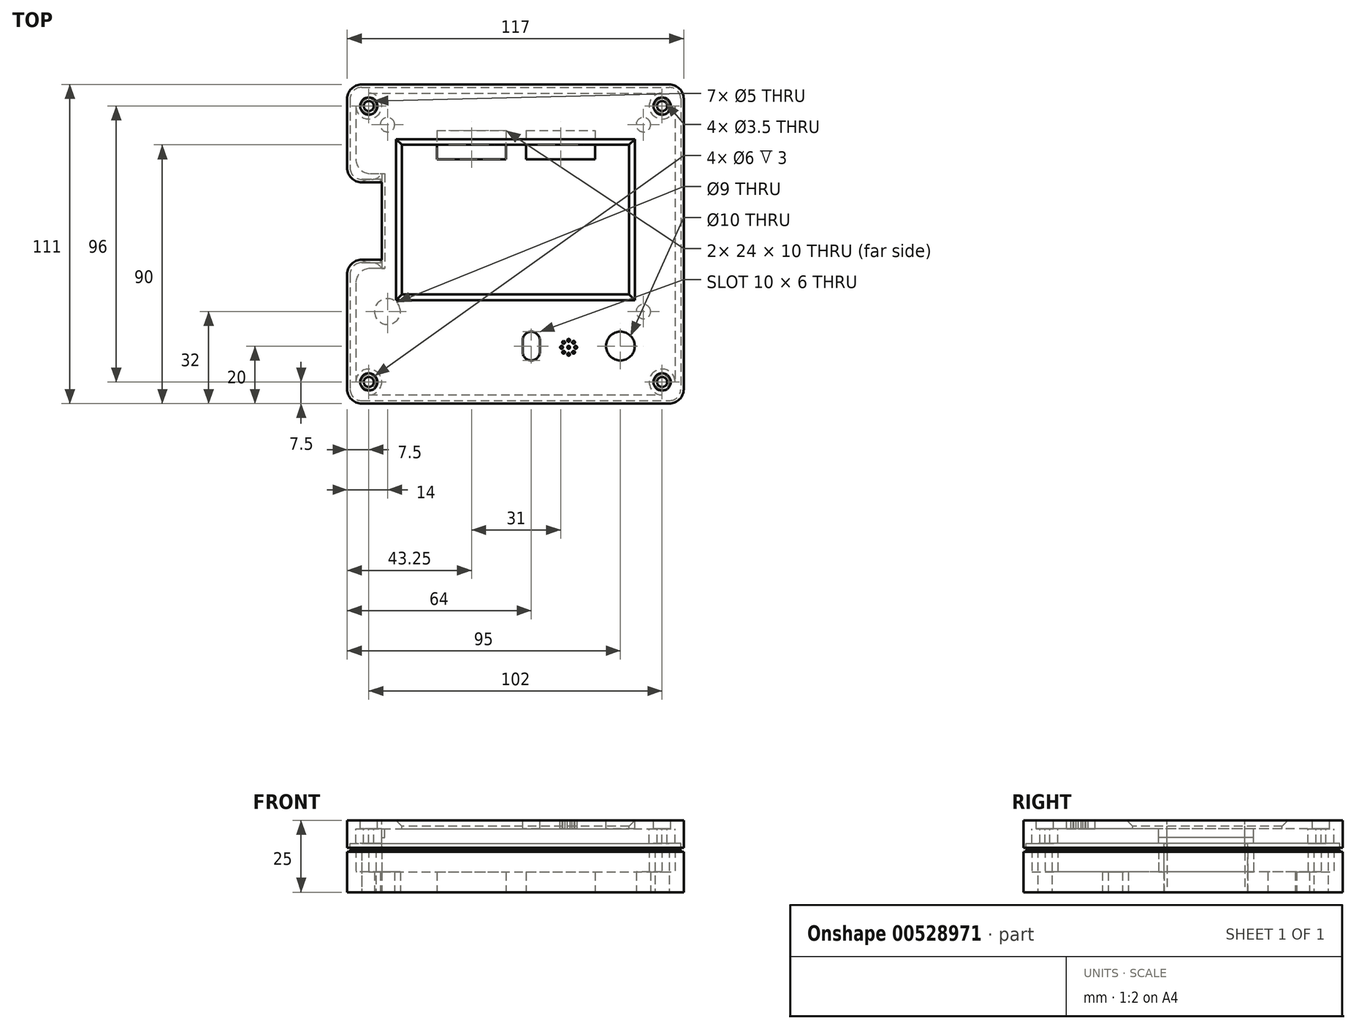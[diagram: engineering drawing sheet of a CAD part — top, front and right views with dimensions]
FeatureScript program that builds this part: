
annotation { "Feature Type Name" : "Feature", "Feature Type Description" : "" }
export const myFeature = defineFeature(function(context is Context, id is Id, definition is map)
    precondition{}
    {
        {
            var Q0;
            Q0=qCreatedBy(makeId("Top.planeOp"),FACE);
            var sketch = newSketch(context, id + "F0", { "sketchPlane" : qUnion([Q0])});
            skLineSegment(sketch, "E0.bottom", {"start": v(-46.5, 43.5) * mm, "end": v(46.5, 43.5) * mm});
            skLineSegment(sketch, "E0.top", {"start": v(-46.5, -43.5) * mm, "end": v(46.5, -43.5) * mm});
            skLineSegment(sketch, "E0.left", {"start": v(-46.5, 43.5) * mm, "end": v(-46.5, -43.5) * mm});
            skLineSegment(sketch, "E0.right", {"start": v(46.5, 43.5) * mm, "end": v(46.5, -43.5) * mm});
            skLineSegment(sketch, "E1.bottom", {"start": v(-51, 52.5) * mm, "end": v(51, 52.5) * mm});
            skLineSegment(sketch, "E1.top", {"start": v(-51, -52.5) * mm, "end": v(51, -52.5) * mm});
            skLineSegment(sketch, "E1.left", {"start": v(-55.5, 48) * mm, "end": v(-55.5, 29.5) * mm});
            skLineSegment(sketch, "E1.right", {"start": v(55.5, 48) * mm, "end": v(55.5, -48) * mm});
            skLineSegment(sketch, "E2.bottom", {"start": v(-53.5, 55.5) * mm, "end": v(53.5, 55.5) * mm});
            skLineSegment(sketch, "E2.top", {"start": v(-53.5, -55.5) * mm, "end": v(53.5, -55.5) * mm});
            skLineSegment(sketch, "E2.left", {"start": v(-58.5, 50.5) * mm, "end": v(-58.5, 26.5) * mm});
            skLineSegment(sketch, "E2.right", {"start": v(58.5, 50.5) * mm, "end": v(58.5, -50.5) * mm});
            skCircle(sketch, "E3", {"center": v(-51, -48) * mm, "radius": 2.5 * mm});
            skCircle(sketch, "E4", {"center": v(51, -48) * mm, "radius": 2.5 * mm});
            skCircle(sketch, "E5", {"center": v(51, 48) * mm, "radius": 2.5 * mm});
            skCircle(sketch, "E6", {"center": v(-51, 48) * mm, "radius": 2.5 * mm});
            skCircle(sketch, "E7", {"center": v(-51, 48) * mm, "radius": 4.5 * mm});
            skCircle(sketch, "E8", {"center": v(-51, -48) * mm, "radius": 4.5 * mm});
            skCircle(sketch, "E9", {"center": v(51, -48) * mm, "radius": 4.5 * mm});
            skCircle(sketch, "E10", {"center": v(51, 48) * mm, "radius": 4.5 * mm});
            skPoint(sketch, "E11.visualSharp", {"position": v(58.5, 55.5) * mm});
            skArc(sketch, "E11.filletArc", {"start": v(58.5, 50.5) * mm, "mid": v(57.04, 54.04) * mm, "end": v(53.5, 55.5) * mm});
            skPoint(sketch, "E12.visualSharp", {"position": v(58.5, -55.5) * mm});
            skArc(sketch, "E12.filletArc", {"start": v(53.5, -55.5) * mm, "mid": v(57.04, -54.04) * mm, "end": v(58.5, -50.5) * mm});
            skPoint(sketch, "E13.visualSharp", {"position": v(-58.5, -55.5) * mm});
            skArc(sketch, "E13.filletArc", {"start": v(-58.5, -50.5) * mm, "mid": v(-57.04, -54.04) * mm, "end": v(-53.5, -55.5) * mm});
            skPoint(sketch, "E14.visualSharp", {"position": v(-58.5, 55.5) * mm});
            skArc(sketch, "E14.filletArc", {"start": v(-53.5, 55.5) * mm, "mid": v(-57.04, 54.04) * mm, "end": v(-58.5, 50.5) * mm});
            skLineSegment(sketch, "E15.bottom", {"start": v(-27.25, 39.5) * mm, "end": v(-3.25, 39.5) * mm});
            skLineSegment(sketch, "E15.top", {"start": v(-27.25, 29.5) * mm, "end": v(-3.25, 29.5) * mm});
            skLineSegment(sketch, "E15.left", {"start": v(-27.25, 39.5) * mm, "end": v(-27.25, 29.5) * mm});
            skLineSegment(sketch, "E15.right", {"start": v(-3.25, 39.5) * mm, "end": v(-3.25, 29.5) * mm});
            skPoint(sketch, "E16.firstSnap0", {"position": v(-15.25, 39.5) * mm});
            skLineSegment(sketch, "E16.bottom", {"start": v(3.75, 39.5) * mm, "end": v(27.75, 39.5) * mm});
            skLineSegment(sketch, "E16.top", {"start": v(3.75, 29.5) * mm, "end": v(27.75, 29.5) * mm});
            skLineSegment(sketch, "E16.left", {"start": v(3.75, 39.5) * mm, "end": v(3.75, 29.5) * mm});
            skLineSegment(sketch, "E16.right", {"start": v(27.75, 39.5) * mm, "end": v(27.75, 29.5) * mm});
            skCircle(sketch, "E17", {"center": v(44.5, 41.5) * mm, "radius": 2.5 * mm});
            skCircle(sketch, "E18", {"center": v(44.5, -23.5) * mm, "radius": 2.5 * mm});
            skCircle(sketch, "E19", {"center": v(-44.5, -23.5) * mm, "radius": 2.5 * mm});
            skCircle(sketch, "E20", {"center": v(-44.5, 41.5) * mm, "radius": 2.5 * mm});
            skCircle(sketch, "E21", {"center": v(-44.5, 41.5) * mm, "radius": 4.5 * mm});
            skCircle(sketch, "E22", {"center": v(44.5, 41.5) * mm, "radius": 4.5 * mm});
            skCircle(sketch, "E23", {"center": v(44.5, -23.5) * mm, "radius": 4.5 * mm});
            skCircle(sketch, "E24", {"center": v(-44.5, -23.5) * mm, "radius": 4.5 * mm});
            skLineSegment(sketch, "E25.bottom", {"start": v(-46.5, 21.5) * mm, "end": v(-53.5, 21.5) * mm});
            skLineSegment(sketch, "E25.top", {"start": v(-46.5, -5.5) * mm, "end": v(-53.5, -5.5) * mm});
            skLineSegment(sketch, "E25.left", {"start": v(-46.5, 21.5) * mm, "end": v(-46.5, -5.5) * mm});
            skLineSegment(sketch, "E26.trimOffspring", {"start": v(-58.5, -10.5) * mm, "end": v(-58.5, -50.5) * mm});
            skLineSegment(sketch, "E27.trimOffspring", {"start": v(-55.5, -13.5) * mm, "end": v(-55.5, -48) * mm});
            skPoint(sketch, "E28.visualSharp", {"position": v(-58.5, 21.5) * mm});
            skArc(sketch, "E28.filletArc", {"start": v(-58.5, 26.5) * mm, "mid": v(-57.04, 22.96) * mm, "end": v(-53.5, 21.5) * mm});
            skPoint(sketch, "E29.visualSharp", {"position": v(-58.5, -5.5) * mm});
            skArc(sketch, "E29.filletArc", {"start": v(-53.5, -5.5) * mm, "mid": v(-57.04, -6.96) * mm, "end": v(-58.5, -10.5) * mm});
            skLineSegment(sketch, "E30.top", {"start": v(-46.5, -8.5) * mm, "end": v(-50.5, -8.5) * mm});
            skLineSegment(sketch, "E30.left", {"start": v(-46.5, -5.5) * mm, "end": v(-46.5, -8.5) * mm});
            skArc(sketch, "E31.filletArc", {"start": v(-50.5, -8.5) * mm, "mid": v(-54.04, -9.96) * mm, "end": v(-55.5, -13.5) * mm});
            skLineSegment(sketch, "E32", {"start": v(-50.5, 24.5) * mm, "end": v(-46.5, 24.5) * mm});
            skPoint(sketch, "E33.visualSharp", {"position": v(-55.5, 24.5) * mm});
            skArc(sketch, "E33.filletArc", {"start": v(-55.5, 29.5) * mm, "mid": v(-54.04, 25.96) * mm, "end": v(-50.5, 24.5) * mm});
            skArc(sketch, "E34.0", {"start": v(-53.5, -6.5) * mm, "mid": v(-56.33, -7.67) * mm, "end": v(-57.5, -10.5) * mm});
            skLineSegment(sketch, "E34.1", {"start": v(-57.5, -10.5) * mm, "end": v(-57.5, -50.5) * mm});
            skArc(sketch, "E34.2", {"start": v(-57.5, -50.5) * mm, "mid": v(-56.33, -53.33) * mm, "end": v(-53.5, -54.5) * mm});
            skLineSegment(sketch, "E34.3", {"start": v(-57.5, 50.5) * mm, "end": v(-57.5, 26.5) * mm});
            skArc(sketch, "E34.4", {"start": v(-57.5, 26.5) * mm, "mid": v(-56.33, 23.67) * mm, "end": v(-53.5, 22.5) * mm});
            skLineSegment(sketch, "E34.5", {"start": v(-46.5, 22.5) * mm, "end": v(-53.5, 22.5) * mm});
            skArc(sketch, "E34.7", {"start": v(-53.5, 54.5) * mm, "mid": v(-56.33, 53.33) * mm, "end": v(-57.5, 50.5) * mm});
            skLineSegment(sketch, "E34.8", {"start": v(-53.5, 54.5) * mm, "end": v(53.5, 54.5) * mm});
            skArc(sketch, "E34.9", {"start": v(57.5, 50.5) * mm, "mid": v(56.33, 53.33) * mm, "end": v(53.5, 54.5) * mm});
            skLineSegment(sketch, "E34.10", {"start": v(57.5, 50.5) * mm, "end": v(57.5, -50.5) * mm});
            skArc(sketch, "E34.11", {"start": v(53.5, -54.5) * mm, "mid": v(56.33, -53.33) * mm, "end": v(57.5, -50.5) * mm});
            skLineSegment(sketch, "E34.12", {"start": v(-53.5, -54.5) * mm, "end": v(53.5, -54.5) * mm});
            skLineSegment(sketch, "E35", {"start": v(-53.5, -6.5) * mm, "end": v(-46.5, -6.5) * mm});
            skLineSegment(sketch, "E36", {"start": v(-53.5, -5.5) * mm, "end": v(-53.5, -6.5) * mm});
            skLineSegment(sketch, "E37", {"start": v(-53.5, 22.5) * mm, "end": v(-53.5, 21.5) * mm});
            skLineSegment(sketch, "E38.bottom", {"start": v(-46.5, 24.5) * mm, "end": v(-43.5, 24.5) * mm});
            skLineSegment(sketch, "E38.top", {"start": v(-46.5, -8.5) * mm, "end": v(-43.5, -8.5) * mm});
            skLineSegment(sketch, "E38.left", {"start": v(-46.5, 24.5) * mm, "end": v(-46.5, -8.5) * mm});
            skLineSegment(sketch, "E38.right", {"start": v(-43.5, 24.5) * mm, "end": v(-43.5, -8.5) * mm});
            skSolve(sketch);
        }
        {
            var Q0;
            {var subQ0=sQuery(id+"F0.wireOp",EDGE,"E1.bottom");Q0=makeQuery(id+"F0.imprint","IMPRINT",FACE,{"disambiguationData":[TD([[makeQuery(id+"F0.imprint","IMPRINT",EDGE,{"derivedFrom":subQ0}),1.0]])]});}
            var Q1;
            Q1=makeQuery(id+"F0.imprint","IMPRINT",FACE,{"disambiguationData":[TD([[makeQuery(id+"F0.imprint","IMPRINT",EDGE,{"derivedFrom":sQuery(id+"F0.wireOp",EDGE,"E6")}),-1.0]])]});
            var Q2;
            Q2=makeQuery(id+"F0.imprint","IMPRINT",FACE,{"disambiguationData":[TD([[makeQuery(id+"F0.imprint","IMPRINT",EDGE,{"derivedFrom":sQuery(id+"F0.wireOp",EDGE,"E5")}),-1.0]])]});
            var Q3;
            Q3=makeQuery(id+"F0.imprint","IMPRINT",FACE,{"disambiguationData":[TD([[makeQuery(id+"F0.imprint","IMPRINT",EDGE,{"derivedFrom":sQuery(id+"F0.wireOp",EDGE,"E4")}),-1.0]])]});
            var Q4;
            Q4=makeQuery(id+"F0.imprint","IMPRINT",FACE,{"disambiguationData":[TD([[makeQuery(id+"F0.imprint","IMPRINT",EDGE,{"derivedFrom":sQuery(id+"F0.wireOp",EDGE,"E3")}),-1.0]])]});
            extrude(context, id + "F1", {"entities" : qUnion([Q0, Q1, Q2, Q3, Q4]), "depth" : 15 * mm});
        }
        {
            var Q0;
            {var subQ1=sQuery(id+"F0.wireOp",EDGE,"E0.left");var subQ5=sQuery(id+"F0.wireOp",EDGE,"E0.bottom");var subQ6=makeQuery(id+"F0.imprint","INTERSECT",VERTEX,{"derivedFrom":[subQ5,subQ1]});Q0=makeQuery(id+"F0.imprint","IMPRINT",FACE,{"disambiguationData":[TD([[makeQuery(id+"F0.imprint","IMPRINT",EDGE,{"disambiguationData":[TD([[subQ6,-1.0]])],"derivedFrom":subQ5}),1.0]])]});}
            var Q1;
            {var subQ0=sQuery(id+"F0.wireOp",EDGE,"E20");var subQ1=sQuery(id+"F0.wireOp",EDGE,"E0.bottom");var subQ2=makeQuery(id+"F0.imprint","INTERSECT",VERTEX,{"disambiguationData":[OD(1.0)],"derivedFrom":[subQ1,subQ0]});Q1=makeQuery(id+"F0.imprint","IMPRINT",FACE,{"disambiguationData":[TD([[makeQuery(id+"F0.imprint","IMPRINT",EDGE,{"disambiguationData":[TD([[subQ2,-1.0]])],"derivedFrom":subQ1}),-1.0]])]});}
            var Q2;
            {var subQ3=sQuery(id+"F0.wireOp",EDGE,"E22");var subQ5=sQuery(id+"F0.wireOp",EDGE,"E0.bottom");var subQ10=makeQuery(id+"F0.imprint","INTERSECT",VERTEX,{"derivedFrom":[subQ5,subQ3]});Q2=makeQuery(id+"F0.imprint","IMPRINT",FACE,{"disambiguationData":[TD([[makeQuery(id+"F0.imprint","IMPRINT",EDGE,{"disambiguationData":[TD([[subQ10,-1.0]])],"derivedFrom":subQ5}),1.0]])]});}
            var Q3;
            {var subQ0=sQuery(id+"F0.wireOp",EDGE,"E22");var subQ1=sQuery(id+"F0.wireOp",EDGE,"E0.bottom");var subQ2=makeQuery(id+"F0.imprint","INTERSECT",VERTEX,{"derivedFrom":[subQ1,subQ0]});Q3=makeQuery(id+"F0.imprint","IMPRINT",FACE,{"disambiguationData":[TD([[makeQuery(id+"F0.imprint","IMPRINT",EDGE,{"disambiguationData":[TD([[subQ2,-1.0]])],"derivedFrom":subQ1}),-1.0]])]});}
            var Q4;
            {var subQ0=sQuery(id+"F0.wireOp",EDGE,"E19");var subQ1=sQuery(id+"F0.wireOp",EDGE,"E0.top");var subQ2=makeQuery(id+"F0.imprint","INTERSECT",VERTEX,{"disambiguationData":[OD(1.0)],"derivedFrom":[subQ1,subQ0]});Q4=makeQuery(id+"F0.imprint","IMPRINT",FACE,{"disambiguationData":[TD([[makeQuery(id+"F0.imprint","IMPRINT",EDGE,{"disambiguationData":[TD([[subQ2,-1.0]])],"derivedFrom":subQ1}),1.0]])]});}
            var Q5;
            {var subQ0=sQuery(id+"F0.wireOp",EDGE,"E24");var subQ1=sQuery(id+"F0.wireOp",EDGE,"E0.left");var subQ2=makeQuery(id+"F0.imprint","INTERSECT",VERTEX,{"disambiguationData":[OD(0.0)],"derivedFrom":[subQ1,subQ0]});Q5=makeQuery(id+"F0.imprint","IMPRINT",FACE,{"disambiguationData":[TD([[makeQuery(id+"F0.imprint","IMPRINT",EDGE,{"disambiguationData":[TD([[subQ2,-1.0]])],"derivedFrom":subQ1}),1.0]])]});}
            var Q6;
            {var subQ0=sQuery(id+"F0.wireOp",EDGE,"E24");var subQ1=sQuery(id+"F0.wireOp",EDGE,"E0.left");var subQ2=makeQuery(id+"F0.imprint","INTERSECT",VERTEX,{"disambiguationData":[OD(0.0)],"derivedFrom":[subQ1,subQ0]});Q6=makeQuery(id+"F0.imprint","IMPRINT",FACE,{"disambiguationData":[TD([[makeQuery(id+"F0.imprint","IMPRINT",EDGE,{"disambiguationData":[TD([[subQ2,-1.0]])],"derivedFrom":subQ1}),-1.0]])]});}
            var Q7;
            {var subQ0=sQuery(id+"F0.wireOp",EDGE,"E23");var subQ1=sQuery(id+"F0.wireOp",EDGE,"E0.right");var subQ2=makeQuery(id+"F0.imprint","INTERSECT",VERTEX,{"disambiguationData":[OD(0.0)],"derivedFrom":[subQ1,subQ0]});Q7=makeQuery(id+"F0.imprint","IMPRINT",FACE,{"disambiguationData":[TD([[makeQuery(id+"F0.imprint","IMPRINT",EDGE,{"disambiguationData":[TD([[subQ2,-1.0]])],"derivedFrom":subQ1}),-1.0]])]});}
            var Q8;
            {var subQ0=sQuery(id+"F0.wireOp",EDGE,"E23");var subQ1=sQuery(id+"F0.wireOp",EDGE,"E0.right");var subQ2=makeQuery(id+"F0.imprint","INTERSECT",VERTEX,{"disambiguationData":[OD(0.0)],"derivedFrom":[subQ1,subQ0]});Q8=makeQuery(id+"F0.imprint","IMPRINT",FACE,{"disambiguationData":[TD([[makeQuery(id+"F0.imprint","IMPRINT",EDGE,{"disambiguationData":[TD([[subQ2,-1.0]])],"derivedFrom":subQ1}),1.0]])]});}
            var Q9;
            {var subQ0=sQuery(id+"F0.wireOp",EDGE,"E0.left");var subQ1=sQuery(id+"F0.wireOp",EDGE,"E0.bottom");var subQ2=makeQuery(id+"F0.imprint","INTERSECT",VERTEX,{"derivedFrom":[subQ1,subQ0]});Q9=makeQuery(id+"F0.imprint","IMPRINT",FACE,{"disambiguationData":[TD([[makeQuery(id+"F0.imprint","IMPRINT",EDGE,{"disambiguationData":[TD([[subQ2,-1.0]])],"derivedFrom":subQ1}),-1.0]])]});}
            var Q10;
            {var subQ0=sQuery(id+"F0.wireOp",EDGE,"E0.right");var subQ1=sQuery(id+"F0.wireOp",EDGE,"E0.bottom");var subQ2=makeQuery(id+"F0.imprint","INTERSECT",VERTEX,{"derivedFrom":[subQ1,subQ0]});Q10=makeQuery(id+"F0.imprint","IMPRINT",FACE,{"disambiguationData":[TD([[makeQuery(id+"F0.imprint","IMPRINT",EDGE,{"disambiguationData":[TD([[subQ2,1.0]])],"derivedFrom":subQ1}),-1.0]])]});}
            var Q11;
            {var subQ3=sQuery(id+"F0.wireOp",EDGE,"E38.bottom");Q11=makeQuery(id+"F0.imprint","IMPRINT",FACE,{"disambiguationData":[TD([[makeQuery(id+"F0.imprint","IMPRINT",EDGE,{"derivedFrom":subQ3}),-1.0]])]});}
            extrude(context, id + "F2", {"entities" : qUnion([Q0, Q1, Q2, Q3, Q4, Q5, Q6, Q7, Q8, Q9, Q10, Q11]), "depth" : 7 * mm});
        }
        {
            var Q0;
            {var subQ0=sQuery(id+"F0.wireOp",EDGE,"E0.right");var subQ1=sQuery(id+"F0.wireOp",EDGE,"E0.bottom");var subQ2=makeQuery(id+"F0.imprint","INTERSECT",VERTEX,{"derivedFrom":[subQ1,subQ0]});Q0=makeQuery(id+"F0.imprint","IMPRINT",FACE,{"disambiguationData":[TD([[makeQuery(id+"F0.imprint","IMPRINT",EDGE,{"disambiguationData":[TD([[subQ2,1.0]])],"derivedFrom":subQ1}),-1.0]])]});}
            var Q1;
            {var subQ2=sQuery(id+"F0.wireOp",EDGE,"E1.bottom");Q1=makeQuery(id+"F0.imprint","IMPRINT",FACE,{"disambiguationData":[TD([[makeQuery(id+"F0.imprint","IMPRINT",EDGE,{"derivedFrom":subQ2}),-1.0]])]});}
            var Q2;
            Q2=makeQuery(id+"F0.imprint","IMPRINT",FACE,{"disambiguationData":[TD([[makeQuery(id+"F0.imprint","IMPRINT",EDGE,{"derivedFrom":sQuery(id+"F0.wireOp",EDGE,"E15.bottom")}),1.0]])]});
            extrude(context, id + "F3", {"entities" : qUnion([Q0, Q1, Q2]), "operationType" : NewBodyOperationType.ADD, "depth" : 3 * mm});
        }
        {
            var Q0;
            {var subQ0=sQuery(id+"F0.wireOp",EDGE,"E34.5");var subQ1=sQuery(id+"F0.wireOp",EDGE,"E38.left");Q0=makeQuery(id+"F3.boolean.opBoolean","SPLIT",EDGE,{"disambiguationData":[topologyDisambiguationEdgeConnected([makeQuery(id+"F2.opExtrude","SWEPT_FACE",FACE,{"disambiguationData":[OSD([subQ1])]})])],"derivedFrom":makeQuery(id+"F1.opExtrude","SWEPT_EDGE",EDGE,{"disambiguationData":[OSD([subQ0,subQ1])]})});}
            var Q1;
            {var subQ0=sQuery(id+"F0.wireOp",EDGE,"E35");var subQ1=sQuery(id+"F0.wireOp",EDGE,"E38.left");Q1=makeQuery(id+"F3.boolean.opBoolean","SPLIT",EDGE,{"disambiguationData":[topologyDisambiguationEdgeConnected([makeQuery(id+"F2.opExtrude","SWEPT_FACE",FACE,{"disambiguationData":[OSD([subQ1])]})])],"derivedFrom":makeQuery(id+"F1.opExtrude","SWEPT_EDGE",EDGE,{"disambiguationData":[OSD([subQ0,subQ1])]})});}
            fillet(context, id + "F4", {"entities" : qUnion([Q0, Q1]), "radius" : 4 * mm, "tangentPropagation" : true, "allowEdgeOverflow" : false});
        }
        {
            var Q0;
            Q0=makeQuery(id+"F0.imprint","IMPRINT",FACE,{"disambiguationData":[TD([[makeQuery(id+"F0.imprint","IMPRINT",EDGE,{"derivedFrom":sQuery(id+"F0.wireOp",EDGE,"E2.bottom")}),-1.0]])]});
            extrude(context, id + "F5", {"entities" : qUnion([Q0]), "operationType" : NewBodyOperationType.ADD, "depth" : 14 * mm});
        }
        {
            var Q0;
            {var subQ0=sQuery(id+"F0.wireOp",EDGE,"E37");var subQ1=sQuery(id+"F0.wireOp",EDGE,"E34.5");var subQ2=sQuery(id+"F0.wireOp",EDGE,"E34.4");Q0=makeQuery(id+"F5.boolean.opBoolean","MERGE",EDGE,{"derivedFrom":[makeQuery(id+"F1.opExtrude","SWEPT_EDGE",EDGE,{"disambiguationData":[OSD([subQ2,subQ1,subQ0])]}),makeQuery(id+"F5.opExtrude","SWEPT_EDGE",EDGE,{"disambiguationData":[OSD([subQ2,subQ1,subQ0])]})]});}
            fillet(context, id + "F6", {"entities" : qUnion([Q0]), "radius" : 5 * mm, "tangentPropagation" : true, "allowEdgeOverflow" : false});
        }
        {
            var Q0;
            {var subQ0=sQuery(id+"F0.wireOp",EDGE,"E36");var subQ1=sQuery(id+"F0.wireOp",EDGE,"E35");var subQ2=sQuery(id+"F0.wireOp",EDGE,"E34.0");Q0=makeQuery(id+"F5.boolean.opBoolean","MERGE",EDGE,{"derivedFrom":[makeQuery(id+"F1.opExtrude","SWEPT_EDGE",EDGE,{"disambiguationData":[OSD([subQ2,subQ1,subQ0])]}),makeQuery(id+"F5.opExtrude","SWEPT_EDGE",EDGE,{"disambiguationData":[OSD([subQ2,subQ1,subQ0])]})]});}
            fillet(context, id + "F7", {"entities" : qUnion([Q0]), "radius" : 5 * mm, "tangentPropagation" : true, "allowEdgeOverflow" : false});
        }
        {
            var Q0;
            Q0=qCreatedBy(makeId("Top.planeOp"),FACE);
            cPlane(context, id + "F8", {"entities" : qUnion([Q0]), "cplaneType" : CPlaneType.OFFSET, "offset" : 25 * mm, "width" : 150 * mm, "height" : 150 * mm});
        }
        {
            var Q0;
            Q0=qCreatedBy(id+"F8.planeOp",FACE);
            var sketch = newSketch(context, id + "F9", { "sketchPlane" : qUnion([Q0])});
            skLineSegment(sketch, "E39.bottom", {"start": v(-46.5, 43.5) * mm, "end": v(46.5, 43.5) * mm});
            skLineSegment(sketch, "E39.top", {"start": v(-46.5, -43.5) * mm, "end": v(46.5, -43.5) * mm});
            skLineSegment(sketch, "E39.left", {"start": v(-46.5, 43.5) * mm, "end": v(-46.5, -43.5) * mm});
            skLineSegment(sketch, "E39.right", {"start": v(46.5, 43.5) * mm, "end": v(46.5, -43.5) * mm});
            skLineSegment(sketch, "E40.bottom", {"start": v(-51, 52.5) * mm, "end": v(51, 52.5) * mm});
            skLineSegment(sketch, "E40.top", {"start": v(-51, -52.5) * mm, "end": v(51, -52.5) * mm});
            skLineSegment(sketch, "E40.left", {"start": v(-55.5, 48) * mm, "end": v(-55.5, 29.5) * mm});
            skLineSegment(sketch, "E40.right", {"start": v(55.5, 48) * mm, "end": v(55.5, -48) * mm});
            skLineSegment(sketch, "E41.bottom", {"start": v(-53.5, 55.5) * mm, "end": v(53.5, 55.5) * mm});
            skLineSegment(sketch, "E41.top", {"start": v(-53.5, -55.5) * mm, "end": v(53.5, -55.5) * mm});
            skLineSegment(sketch, "E41.left", {"start": v(-58.5, 50.5) * mm, "end": v(-58.5, 26.5) * mm});
            skLineSegment(sketch, "E41.right", {"start": v(58.5, 50.5) * mm, "end": v(58.5, -50.5) * mm});
            skCircle(sketch, "E42", {"center": v(-51, -48) * mm, "radius": 1.75 * mm});
            skCircle(sketch, "E43", {"center": v(51, -48) * mm, "radius": 1.75 * mm});
            skCircle(sketch, "E44", {"center": v(51, 48) * mm, "radius": 1.75 * mm});
            skCircle(sketch, "E45", {"center": v(-51, 48) * mm, "radius": 1.75 * mm});
            skArc(sketch, "E46", {"start": v(-51, 52.5) * mm, "mid": v(-54.18, 51.18) * mm, "end": v(-55.5, 48) * mm});
            skArc(sketch, "E47", {"start": v(-55.5, -48) * mm, "mid": v(-54.18, -51.18) * mm, "end": v(-51, -52.5) * mm});
            skArc(sketch, "E48", {"start": v(51, -52.5) * mm, "mid": v(54.18, -51.18) * mm, "end": v(55.5, -48) * mm});
            skArc(sketch, "E49", {"start": v(55.5, 48) * mm, "mid": v(54.18, 51.18) * mm, "end": v(51, 52.5) * mm});
            skPoint(sketch, "E50.visualSharp", {"position": v(58.5, 55.5) * mm});
            skArc(sketch, "E50.filletArc", {"start": v(58.5, 50.5) * mm, "mid": v(57.04, 54.04) * mm, "end": v(53.5, 55.5) * mm});
            skPoint(sketch, "E51.visualSharp", {"position": v(58.5, -55.5) * mm});
            skArc(sketch, "E51.filletArc", {"start": v(53.5, -55.5) * mm, "mid": v(57.04, -54.04) * mm, "end": v(58.5, -50.5) * mm});
            skPoint(sketch, "E52.visualSharp", {"position": v(-58.5, -55.5) * mm});
            skArc(sketch, "E52.filletArc", {"start": v(-58.5, -50.5) * mm, "mid": v(-57.04, -54.04) * mm, "end": v(-53.5, -55.5) * mm});
            skPoint(sketch, "E53.visualSharp", {"position": v(-58.5, 55.5) * mm});
            skArc(sketch, "E53.filletArc", {"start": v(-53.5, 55.5) * mm, "mid": v(-57.04, 54.04) * mm, "end": v(-58.5, 50.5) * mm});
            skLineSegment(sketch, "E54.bottom", {"start": v(-46.5, 21.5) * mm, "end": v(-53.5, 21.5) * mm});
            skLineSegment(sketch, "E54.top", {"start": v(-46.5, -5.5) * mm, "end": v(-53.5, -5.5) * mm});
            skLineSegment(sketch, "E54.left", {"start": v(-46.5, 21.5) * mm, "end": v(-46.5, -5.5) * mm});
            skLineSegment(sketch, "E55.trimOffspring", {"start": v(-58.5, -10.5) * mm, "end": v(-58.5, -50.5) * mm});
            skLineSegment(sketch, "E56.trimOffspring", {"start": v(-55.5, -13.5) * mm, "end": v(-55.5, -48) * mm});
            skPoint(sketch, "E57.visualSharp", {"position": v(-58.5, 21.5) * mm});
            skArc(sketch, "E57.filletArc", {"start": v(-58.5, 26.5) * mm, "mid": v(-57.04, 22.96) * mm, "end": v(-53.5, 21.5) * mm});
            skPoint(sketch, "E58.visualSharp", {"position": v(-58.5, -5.5) * mm});
            skArc(sketch, "E58.filletArc", {"start": v(-53.5, -5.5) * mm, "mid": v(-57.04, -6.96) * mm, "end": v(-58.5, -10.5) * mm});
            skLineSegment(sketch, "E59.top", {"start": v(-46.5, -8.5) * mm, "end": v(-50.5, -8.5) * mm});
            skLineSegment(sketch, "E59.left", {"start": v(-46.5, -5.5) * mm, "end": v(-46.5, -8.5) * mm});
            skArc(sketch, "E60.filletArc", {"start": v(-50.5, -8.5) * mm, "mid": v(-54.04, -9.96) * mm, "end": v(-55.5, -13.5) * mm});
            skLineSegment(sketch, "E61", {"start": v(-50.5, 24.5) * mm, "end": v(-46.5, 24.5) * mm});
            skPoint(sketch, "E62.visualSharp", {"position": v(-55.5, 24.5) * mm});
            skArc(sketch, "E62.filletArc", {"start": v(-55.5, 29.5) * mm, "mid": v(-54.04, 25.96) * mm, "end": v(-50.5, 24.5) * mm});
            skArc(sketch, "E63.0", {"start": v(-53.5, -6.5) * mm, "mid": v(-56.33, -7.67) * mm, "end": v(-57.5, -10.5) * mm});
            skLineSegment(sketch, "E63.1", {"start": v(-57.5, -10.5) * mm, "end": v(-57.5, -50.5) * mm});
            skArc(sketch, "E63.2", {"start": v(-57.5, -50.5) * mm, "mid": v(-56.33, -53.33) * mm, "end": v(-53.5, -54.5) * mm});
            skLineSegment(sketch, "E63.3", {"start": v(-57.5, 50.5) * mm, "end": v(-57.5, 26.5) * mm});
            skArc(sketch, "E63.4", {"start": v(-57.5, 26.5) * mm, "mid": v(-56.33, 23.67) * mm, "end": v(-53.5, 22.5) * mm});
            skLineSegment(sketch, "E63.5", {"start": v(-46.5, 22.5) * mm, "end": v(-53.5, 22.5) * mm});
            skArc(sketch, "E63.7", {"start": v(-53.5, 54.5) * mm, "mid": v(-56.33, 53.33) * mm, "end": v(-57.5, 50.5) * mm});
            skLineSegment(sketch, "E63.8", {"start": v(-53.5, 54.5) * mm, "end": v(53.5, 54.5) * mm});
            skArc(sketch, "E63.9", {"start": v(57.5, 50.5) * mm, "mid": v(56.33, 53.33) * mm, "end": v(53.5, 54.5) * mm});
            skLineSegment(sketch, "E63.10", {"start": v(57.5, 50.5) * mm, "end": v(57.5, -50.5) * mm});
            skArc(sketch, "E63.11", {"start": v(53.5, -54.5) * mm, "mid": v(56.33, -53.33) * mm, "end": v(57.5, -50.5) * mm});
            skLineSegment(sketch, "E63.12", {"start": v(-53.5, -54.5) * mm, "end": v(53.5, -54.5) * mm});
            skLineSegment(sketch, "E64", {"start": v(-53.5, -6.5) * mm, "end": v(-46.5, -6.5) * mm});
            skLineSegment(sketch, "E65", {"start": v(-53.5, -5.5) * mm, "end": v(-53.5, -6.5) * mm});
            skLineSegment(sketch, "E66", {"start": v(-53.5, 22.5) * mm, "end": v(-53.5, 21.5) * mm});
            skLineSegment(sketch, "E67.bottom", {"start": v(-39.5, 34.5) * mm, "end": v(39.5, 34.5) * mm});
            skLineSegment(sketch, "E67.top", {"start": v(-39.5, -17.5) * mm, "end": v(39.5, -17.5) * mm});
            skLineSegment(sketch, "E67.left", {"start": v(-39.5, 34.5) * mm, "end": v(-39.5, -17.5) * mm});
            skLineSegment(sketch, "E67.right", {"start": v(39.5, 34.5) * mm, "end": v(39.5, -17.5) * mm});
            skCircle(sketch, "E68", {"center": v(36.5, -35.5) * mm, "radius": 5 * mm});
            skArc(sketch, "E69", {"start": v(8.5, -33.5) * mm, "mid": v(5.5, -30.5) * mm, "end": v(2.5, -33.5) * mm});
            skArc(sketch, "E70", {"start": v(2.5, -37.5) * mm, "mid": v(5.5, -40.5) * mm, "end": v(8.5, -37.5) * mm});
            skLineSegment(sketch, "E71.left", {"start": v(2.5, -33.5) * mm, "end": v(2.5, -37.5) * mm});
            skLineSegment(sketch, "E71.right", {"start": v(8.5, -33.5) * mm, "end": v(8.5, -37.5) * mm});
            skCircle(sketch, "E72", {"center": v(18.5, -35.94) * mm, "radius": 0.5 * mm});
            skCircle(sketch, "E73", {"center": v(18.5, -33.5) * mm, "radius": 0.5 * mm});
            skCircle(sketch, "E74.1.0", {"center": v(16.77, -34.21) * mm, "radius": 0.5 * mm});
            skCircle(sketch, "E74.2.0", {"center": v(16.06, -35.94) * mm, "radius": 0.5 * mm});
            skCircle(sketch, "E75.1.3.0", {"center": v(16.77, -37.67) * mm, "radius": 0.5 * mm});
            skCircle(sketch, "E75.1.4.0", {"center": v(18.5, -38.38) * mm, "radius": 0.5 * mm});
            skCircle(sketch, "E75.1.5.0", {"center": v(20.23, -37.67) * mm, "radius": 0.5 * mm});
            skCircle(sketch, "E75.1.6.0", {"center": v(20.94, -35.94) * mm, "radius": 0.5 * mm});
            skCircle(sketch, "E75.1.7.0", {"center": v(20.23, -34.21) * mm, "radius": 0.5 * mm});
            skCircle(sketch, "E76", {"center": v(51, -48) * mm, "radius": 4.5 * mm});
            skCircle(sketch, "E77", {"center": v(-51, -48) * mm, "radius": 4.5 * mm});
            skCircle(sketch, "E78", {"center": v(-51, 48) * mm, "radius": 4.5 * mm});
            skCircle(sketch, "E79", {"center": v(51, 48) * mm, "radius": 4.5 * mm});
            skLineSegment(sketch, "E80.bottom", {"start": v(-46.5, 24.5) * mm, "end": v(-45.5, 24.5) * mm});
            skLineSegment(sketch, "E80.top", {"start": v(-46.5, -8.5) * mm, "end": v(-45.5, -8.5) * mm});
            skLineSegment(sketch, "E80.left", {"start": v(-46.5, 24.5) * mm, "end": v(-46.5, -8.5) * mm});
            skLineSegment(sketch, "E80.right", {"start": v(-45.5, 24.5) * mm, "end": v(-45.5, -8.5) * mm});
            skSolve(sketch);
        }
        {
            var Q0;
            Q0=makeQuery(id+"F9.imprint","IMPRINT",FACE,{"disambiguationData":[TD([[makeQuery(id+"F9.imprint","IMPRINT",EDGE,{"derivedFrom":sQuery(id+"F9.wireOp",EDGE,"E41.bottom")}),-1.0]])]});
            var Q1;
            {var subQ0=sQuery(id+"F9.wireOp",EDGE,"E54.bottom");Q1=makeQuery(id+"F9.imprint","IMPRINT",FACE,{"disambiguationData":[TD([[makeQuery(id+"F9.imprint","IMPRINT",EDGE,{"derivedFrom":subQ0}),-1.0]])]});}
            var Q2;
            Q2=makeQuery(id+"F9.imprint","IMPRINT",FACE,{"disambiguationData":[TD([[makeQuery(id+"F9.imprint","IMPRINT",EDGE,{"derivedFrom":sQuery(id+"F9.wireOp",EDGE,"E40.bottom")}),1.0]])]});
            var Q3;
            {var subQ0=sQuery(id+"F9.wireOp",EDGE,"E54.top");Q3=makeQuery(id+"F9.imprint","IMPRINT",FACE,{"disambiguationData":[TD([[makeQuery(id+"F9.imprint","IMPRINT",EDGE,{"derivedFrom":subQ0}),1.0]])]});}
            extrude(context, id + "F10", {"entities" : qUnion([Q0, Q1, Q2, Q3]), "oppositeDirection" : true, "depth" : (8) * mm});
        }
        {
            var Q0;
            {var subQ1=sQuery(id+"F9.wireOp",EDGE,"E39.bottom");Q0=makeQuery(id+"F9.imprint","IMPRINT",FACE,{"disambiguationData":[TD([[makeQuery(id+"F9.imprint","IMPRINT",EDGE,{"derivedFrom":subQ1}),1.0]])]});}
            var Q1;
            {var subQ6=sQuery(id+"F9.wireOp",EDGE,"E39.bottom");Q1=makeQuery(id+"F9.imprint","IMPRINT",FACE,{"disambiguationData":[TD([[makeQuery(id+"F9.imprint","IMPRINT",EDGE,{"derivedFrom":subQ6}),-1.0]])]});}
            extrude(context, id + "F11", {"entities" : qUnion([Q0, Q1]), "operationType" : NewBodyOperationType.ADD, "oppositeDirection" : true, "depth" : 3 * mm});
        }
        {
            var Q0;
            Q0=makeQuery(id+"F11.opExtrude","CAP_EDGE",EDGE,{"disambiguationData":[OSD([sQuery(id+"F9.wireOp",EDGE,"E67.bottom")])],"isStart":true});
            var Q1;
            Q1=makeQuery(id+"F11.opExtrude","CAP_EDGE",EDGE,{"disambiguationData":[OSD([sQuery(id+"F9.wireOp",EDGE,"E67.left")])],"isStart":true});
            var Q2;
            Q2=makeQuery(id+"F11.opExtrude","CAP_EDGE",EDGE,{"disambiguationData":[OSD([sQuery(id+"F9.wireOp",EDGE,"E67.top")])],"isStart":true});
            var Q3;
            Q3=makeQuery(id+"F11.opExtrude","CAP_EDGE",EDGE,{"disambiguationData":[OSD([sQuery(id+"F9.wireOp",EDGE,"E67.right")])],"isStart":true});
            chamfer(context, id + "F12", {"entities" : qUnion([Q0, Q1, Q2, Q3]), "width" : 2 * mm, "tangentPropagation" : true});
        }
        {
            var Q0;
            Q0=makeQuery(id+"F9.imprint","IMPRINT",FACE,{"disambiguationData":[TD([[makeQuery(id+"F9.imprint","IMPRINT",EDGE,{"derivedFrom":sQuery(id+"F9.wireOp",EDGE,"E41.bottom")}),-1.0]])]});
            var Q1;
            {var subQ0=sQuery(id+"F9.wireOp",EDGE,"E54.top");Q1=makeQuery(id+"F9.imprint","IMPRINT",FACE,{"disambiguationData":[TD([[makeQuery(id+"F9.imprint","IMPRINT",EDGE,{"derivedFrom":subQ0}),1.0]])]});}
            var Q2;
            {var subQ0=sQuery(id+"F9.wireOp",EDGE,"E54.bottom");Q2=makeQuery(id+"F9.imprint","IMPRINT",FACE,{"disambiguationData":[TD([[makeQuery(id+"F9.imprint","IMPRINT",EDGE,{"derivedFrom":subQ0}),-1.0]])]});}
            extrude(context, id + "F13", {"entities" : qUnion([Q0, Q1, Q2]), "operationType" : NewBodyOperationType.ADD, "oppositeDirection" : true, "depth" : 9.5 * mm});
        }
        {
            var Q0;
            Q0=makeQuery(id+"F13.opExtrude","CAP_EDGE",EDGE,{"disambiguationData":[OSD([sQuery(id+"F9.wireOp",EDGE,"E63.3")])],"isStart":false});
            fillet(context, id + "F14", {"entities" : qUnion([Q0]), "radius" : 0.5 * mm, "tangentPropagation" : true, "allowEdgeOverflow" : false});
        }
        {
            var Q0;
            Q0=makeQuery(id+"F1.opExtrude","CAP_EDGE",EDGE,{"disambiguationData":[OSD([sQuery(id+"F0.wireOp",EDGE,"E34.8")])],"isStart":false});
            fillet(context, id + "F15", {"entities" : qUnion([Q0]), "radius" : .5 * mm, "tangentPropagation" : true, "allowEdgeOverflow" : false});
        }
        {
            var Q0;
            Q0=makeQuery(id+"F9.imprint","IMPRINT",FACE,{"disambiguationData":[TD([[makeQuery(id+"F9.imprint","IMPRINT",EDGE,{"derivedFrom":sQuery(id+"F9.wireOp",EDGE,"E44")}),-1.0]])]});
            var Q1;
            Q1=makeQuery(id+"F9.imprint","IMPRINT",FACE,{"disambiguationData":[TD([[makeQuery(id+"F9.imprint","IMPRINT",EDGE,{"derivedFrom":sQuery(id+"F9.wireOp",EDGE,"E45")}),-1.0]])]});
            var Q2;
            Q2=makeQuery(id+"F9.imprint","IMPRINT",FACE,{"disambiguationData":[TD([[makeQuery(id+"F9.imprint","IMPRINT",EDGE,{"derivedFrom":sQuery(id+"F9.wireOp",EDGE,"E43")}),-1.0]])]});
            var Q3;
            Q3=makeQuery(id+"F9.imprint","IMPRINT",FACE,{"disambiguationData":[TD([[makeQuery(id+"F9.imprint","IMPRINT",EDGE,{"derivedFrom":sQuery(id+"F9.wireOp",EDGE,"E42")}),-1.0]])]});
            var Q4;
            {var subQ3=sQuery(id+"F9.wireOp",EDGE,"E80.bottom");Q4=makeQuery(id+"F9.imprint","IMPRINT",FACE,{"disambiguationData":[TD([[makeQuery(id+"F9.imprint","IMPRINT",EDGE,{"derivedFrom":subQ3}),-1.0]])]});}
            extrude(context, id + "F16", {"entities" : qUnion([Q0, Q1, Q2, Q3, Q4]), "operationType" : NewBodyOperationType.ADD, "oppositeDirection" : true, "depth" : 8 * mm});
        }
        {
            var Q0;
            {var subQ8=sQuery(id+"F9.wireOp",EDGE,"E39.bottom");Q0=makeQuery(id+"F9.imprint","IMPRINT",FACE,{"disambiguationData":[TD([[makeQuery(id+"F9.imprint","IMPRINT",EDGE,{"derivedFrom":subQ8}),1.0]])]});}
            var sketch = newSketch(context, id + "F17", { "sketchPlane" : qUnion([Q0])});
            skCircle(sketch, "E81", {"center": v(51, -48) * mm, "radius": 3 * mm});
            skCircle(sketch, "E82", {"center": v(51, 48) * mm, "radius": 3 * mm});
            skCircle(sketch, "E83", {"center": v(-51, 48) * mm, "radius": 3 * mm});
            skCircle(sketch, "E84", {"center": v(-51, -48) * mm, "radius": 3 * mm});
            skSolve(sketch);
        }
        {
            var Q0;
            Q0=makeQuery(id+"F17.imprint","IMPRINT",FACE,{"disambiguationData":[TD([[makeQuery(id+"F17.imprint","IMPRINT",EDGE,{"derivedFrom":sQuery(id+"F17.wireOp",EDGE,"E82")}),1.0]])]});
            var Q1;
            Q1=makeQuery(id+"F17.imprint","IMPRINT",FACE,{"disambiguationData":[TD([[makeQuery(id+"F17.imprint","IMPRINT",EDGE,{"derivedFrom":sQuery(id+"F17.wireOp",EDGE,"E83")}),1.0]])]});
            var Q2;
            Q2=makeQuery(id+"F17.imprint","IMPRINT",FACE,{"disambiguationData":[TD([[makeQuery(id+"F17.imprint","IMPRINT",EDGE,{"derivedFrom":sQuery(id+"F17.wireOp",EDGE,"E84")}),1.0]])]});
            var Q3;
            Q3=makeQuery(id+"F17.imprint","IMPRINT",FACE,{"disambiguationData":[TD([[makeQuery(id+"F17.imprint","IMPRINT",EDGE,{"derivedFrom":sQuery(id+"F17.wireOp",EDGE,"E81")}),1.0]])]});
            extrude(context, id + "F18", {"entities" : qUnion([Q0, Q1, Q2, Q3]), "operationType" : NewBodyOperationType.REMOVE, "oppositeDirection" : true, "depth" : 3 * mm});
        }
        {
            var Q0;
            {var subQ0=sQuery(id+"F9.wireOp",EDGE,"E54.bottom");var subQ1=sQuery(id+"F9.wireOp",EDGE,"E80.left");Q0=makeQuery(id+"F16.boolean.opBoolean","SPLIT",EDGE,{"disambiguationData":[topologyDisambiguationEdgeConnected([makeQuery(id+"F16.opExtrude","SWEPT_FACE",FACE,{"disambiguationData":[OSD([subQ1])]})])],"derivedFrom":makeQuery(id+"F13.boolean.opBoolean","MERGE",EDGE,{"derivedFrom":[makeQuery(id+"F10.opExtrude","SWEPT_EDGE",EDGE,{"disambiguationData":[OSD([subQ0,subQ1])]}),makeQuery(id+"F13.opExtrude","SWEPT_EDGE",EDGE,{"disambiguationData":[OSD([subQ0,subQ1])]})]})});}
            var Q1;
            {var subQ0=sQuery(id+"F9.wireOp",EDGE,"E54.top");var subQ1=sQuery(id+"F9.wireOp",EDGE,"E80.left");Q1=makeQuery(id+"F16.boolean.opBoolean","SPLIT",EDGE,{"disambiguationData":[topologyDisambiguationEdgeConnected([makeQuery(id+"F16.opExtrude","SWEPT_FACE",FACE,{"disambiguationData":[OSD([subQ1])]})])],"derivedFrom":makeQuery(id+"F13.boolean.opBoolean","MERGE",EDGE,{"derivedFrom":[makeQuery(id+"F10.opExtrude","SWEPT_EDGE",EDGE,{"disambiguationData":[OSD([subQ0,subQ1])]}),makeQuery(id+"F13.opExtrude","SWEPT_EDGE",EDGE,{"disambiguationData":[OSD([subQ0,subQ1])]})]})});}
            fillet(context, id + "F19", {"entities" : qUnion([Q0, Q1]), "radius" : 2 * mm, "tangentPropagation" : true, "allowEdgeOverflow" : false});
        }
        {
            var Q0;
            Q0=makeQuery(id+"F16.opExtrude","SWEPT_FACE",FACE,{"disambiguationData":[OSD([sQuery(id+"F9.wireOp",EDGE,"E80.right")])]});
            var sketch = newSketch(context, id + "F20", { "sketchPlane" : qUnion([Q0])});
            skLineSegment(sketch, "E85.bottom", {"start": v(24.5, 17) * mm, "end": v(-8.5, 17) * mm});
            skLineSegment(sketch, "E85.top", {"start": v(24.5, 19) * mm, "end": v(-8.5, 19) * mm});
            skLineSegment(sketch, "E85.left", {"start": v(24.5, 17) * mm, "end": v(24.5, 19) * mm});
            skLineSegment(sketch, "E85.right", {"start": v(-8.5, 17) * mm, "end": v(-8.5, 19) * mm});
            skSolve(sketch);
        }
        {
            var Q0;
            Q0=makeQuery(id+"F20.imprint","IMPRINT",FACE,{"disambiguationData":[TD([[makeQuery(id+"F20.imprint","IMPRINT",EDGE,{"derivedFrom":sQuery(id+"F20.wireOp",EDGE,"E85.bottom")}),-1.0]])]});
            extrude(context, id + "F21", {"entities" : qUnion([Q0]), "operationType" : NewBodyOperationType.REMOVE, "oppositeDirection" : true, "depth" : 1 * mm});
        }
    });
